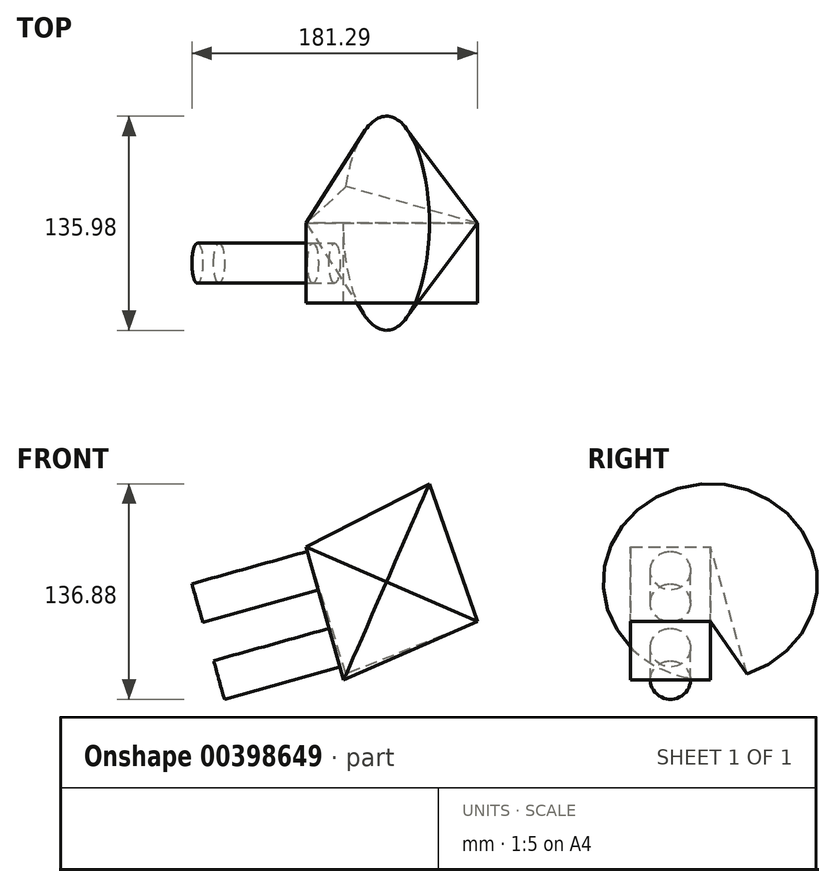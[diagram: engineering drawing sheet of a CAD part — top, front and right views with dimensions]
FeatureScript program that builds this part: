
annotation { "Feature Type Name" : "Feature", "Feature Type Description" : "" }
export const myFeature = defineFeature(function(context is Context, id is Id, definition is map)
    precondition{}
    {
        {
            var Q0;
            Q0=qCreatedBy(makeId("Front.planeOp"),FACE);
            var sketch = newSketch(context, id + "F0", { "sketchPlane" : qUnion([Q0])});
            skLineSegment(sketch, "E0", {"start": v(-62.5, 56.03) * mm, "end": v(46.24, 8.54) * mm});
            skLineSegment(sketch, "E1", {"start": v(46.24, 8.54) * mm, "end": v(-38.74, -28.54) * mm});
            skLineSegment(sketch, "E2", {"start": v(-38.74, -28.54) * mm, "end": v(-62.5, 56.03) * mm});
            skLineSegment(sketch, "E3", {"start": v(59.57, 0) * mm, "end": v(59.57, 76.45) * mm});
            skSolve(sketch);
        }
        {
            var Q0;
            Q0 = qSketchRegion(id + "F0", true);
            extrude(context, id + "F1", {"entities" : qUnion([Q0]), "depth" : 50.8 * mm});
        }
        {
            var Q0;
            Q0=makeQuery(id+"F0.imprint","IMPRINT",FACE,{"disambiguationData":[TD([[makeQuery(id+"F0.imprint","IMPRINT",EDGE,{"derivedFrom":sQuery(id+"F0.wireOp",EDGE,"E0")}),-1.0]])]});
            var Q1;
            Q1=sQuery(id+"F0.wireOp",EDGE,"E0");
            revolve(context, id + "F2", {"entities" : qUnion([Q0]), "axis" : qUnion([Q1]), "revolveType" : RevolveType.ONE_DIRECTION, "oppositeDirection" : true, "angle" : 340 * degree});
        }
        {
            var Q0;
            Q0=makeQuery(id+"F1.opExtrude","SWEPT_FACE",FACE,{"disambiguationData":[OSD([sQuery(id+"F0.wireOp",EDGE,"E2")])]});
            var sketch = newSketch(context, id + "F3", { "sketchPlane" : qUnion([Q0])});
            skCircle(sketch, "E4", {"center": v(25.4, 55.16) * mm, "radius": 12.7 * mm});
            skCircle(sketch, "E5", {"center": v(25.4, 4.36) * mm, "radius": 12.7 * mm});
            skLineSegment(sketch, "E6", {"start": v(-12.14, 3.49) * mm, "end": v(-12.14, 95.85) * mm});
            skPoint(sketch, "E7.0", {"position": v(50.8, 70.84) * mm});
            skPoint(sketch, "E8.0", {"position": v(0, -16.1) * mm});
            skLineSegment(sketch, "E9", {"start": v(50.8, 70.84) * mm, "end": v(0, -16.1) * mm, "construction": true});
            skPoint(sketch, "E10", {"position": v(25.4, 27.37) * mm});
            skLineSegment(sketch, "E11", {"start": v(25.4, 50.38) * mm, "end": v(25.4, 4.36) * mm, "construction": true});
            skSolve(sketch);
        }
        {
            var Q0;
            Q0=makeQuery(id+"F3.imprint","IMPRINT",FACE,{"disambiguationData":[TD([[makeQuery(id+"F3.imprint","IMPRINT",EDGE,{"derivedFrom":sQuery(id+"F3.wireOp",EDGE,"E5")}),1.0]])]});
            var Q1;
            Q1=makeQuery(id+"F3.imprint","IMPRINT",FACE,{"disambiguationData":[TD([[makeQuery(id+"F3.imprint","IMPRINT",EDGE,{"derivedFrom":sQuery(id+"F3.wireOp",EDGE,"E4")}),1.0]])]});
            extrude(context, id + "F4", {"entities" : qUnion([Q0, Q1]), "operationType" : NewBodyOperationType.ADD, "depth" : 76.2 * mm});
        }
    });
